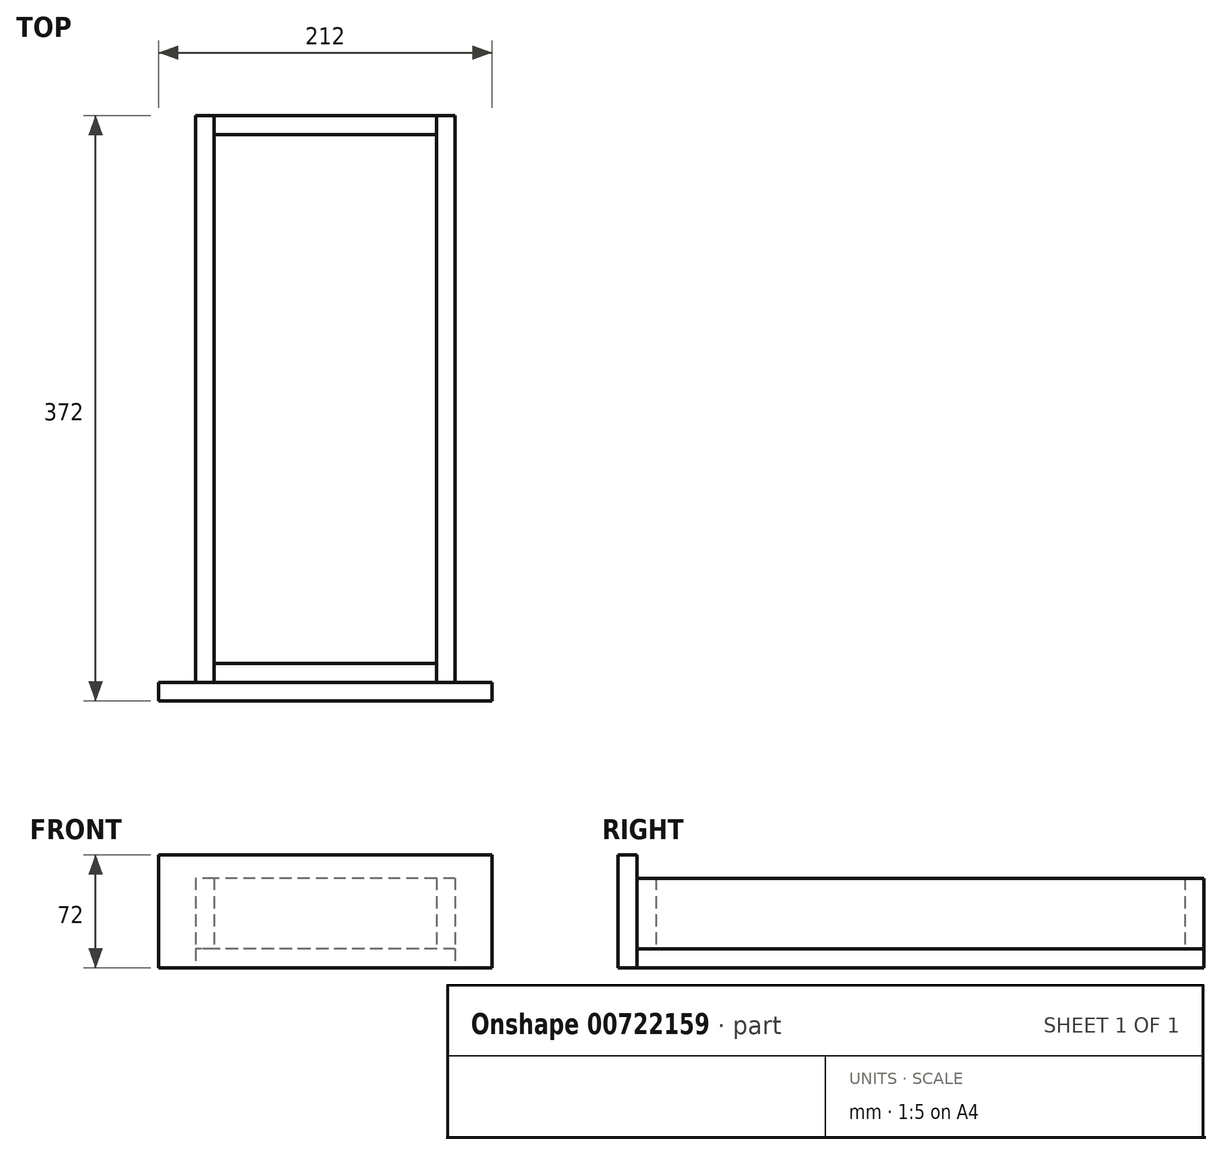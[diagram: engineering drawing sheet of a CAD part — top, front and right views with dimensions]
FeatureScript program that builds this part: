
annotation { "Feature Type Name" : "Feature", "Feature Type Description" : "" }
export const myFeature = defineFeature(function(context is Context, id is Id, definition is map)
    precondition{}
    {
        {
            var Q0;
            Q0=qCreatedBy(makeId("Top.planeOp"),FACE);
            var sketch = newSketch(context, id + "F0", { "sketchPlane" : qUnion([Q0])});
            skLineSegment(sketch, "E0.bottom", {"start": v(82.5, -180) * mm, "end": v(-82.5, -180) * mm});
            skLineSegment(sketch, "E0.top", {"start": v(82.5, 180) * mm, "end": v(-82.5, 180) * mm});
            skLineSegment(sketch, "E0.left", {"start": v(82.5, -180) * mm, "end": v(82.5, 180) * mm});
            skLineSegment(sketch, "E0.right", {"start": v(-82.5, -180) * mm, "end": v(-82.5, 180) * mm});
            skPoint(sketch, "E0.middle", {"position": v(0, 0) * mm});
            skSolve(sketch);
        }
        {
            var Q0;
            Q0 = qSketchRegion(id + "F0", true);
            extrude(context, id + "F1", {"entities" : qUnion([Q0]), "depth" : 12 * mm, "offsetDistance" : 25 * mm});
        }
        {
            var Q0;
            Q0=makeQuery(id+"F1.opExtrude","CAP_FACE",FACE,{"disambiguationData":[OSD([sQuery(id+"F0.wireOp",EDGE,"E0.bottom"),sQuery(id+"F0.wireOp",EDGE,"E0.top"),sQuery(id+"F0.wireOp",EDGE,"E0.left"),sQuery(id+"F0.wireOp",EDGE,"E0.right")])],"isStart":false});
            var sketch = newSketch(context, id + "F2", { "sketchPlane" : qUnion([Q0])});
            skLineSegment(sketch, "E1.0", {"start": v(-82.5, -180) * mm, "end": v(-82.5, 180) * mm});
            skLineSegment(sketch, "E2.0", {"start": v(82.5, 180) * mm, "end": v(-82.5, 180) * mm});
            skLineSegment(sketch, "E3.0", {"start": v(82.5, -180) * mm, "end": v(82.5, 180) * mm});
            skLineSegment(sketch, "E4.0", {"start": v(82.5, -180) * mm, "end": v(-82.5, -180) * mm});
            skLineSegment(sketch, "E5", {"start": v(-70.5, 180) * mm, "end": v(-70.5, -180) * mm});
            skLineSegment(sketch, "E6", {"start": v(70.5, 180) * mm, "end": v(70.5, -180) * mm});
            skLineSegment(sketch, "E7", {"start": v(-70.5, -168) * mm, "end": v(70.5, -168) * mm});
            skLineSegment(sketch, "E8", {"start": v(-70.5, 168) * mm, "end": v(70.5, 168) * mm});
            skSolve(sketch);
        }
        {
            var Q0;
            {var subQ5=sQuery(id+"F2.wireOp",EDGE,"E8");Q0=makeQuery(id+"F2.imprint","IMPRINT",FACE,{"disambiguationData":[TD([[makeQuery(id+"F2.imprint","IMPRINT",EDGE,{"derivedFrom":subQ5}),1.0]])]});}
            var Q1;
            {var subQ5=sQuery(id+"F2.wireOp",EDGE,"E7");Q1=makeQuery(id+"F2.imprint","IMPRINT",FACE,{"disambiguationData":[TD([[makeQuery(id+"F2.imprint","IMPRINT",EDGE,{"derivedFrom":subQ5}),-1.0]])]});}
            extrude(context, id + "F3", {"entities" : qUnion([Q0, Q1]), "depth" : 45 * mm, "offsetDistance" : 25 * mm});
        }
        {
            var Q0;
            {var subQ1=sQuery(id+"F2.wireOp",EDGE,"E1.0");Q0=makeQuery(id+"F2.imprint","IMPRINT",FACE,{"disambiguationData":[TD([[makeQuery(id+"F2.imprint","IMPRINT",EDGE,{"derivedFrom":subQ1}),-1.0]])]});}
            var Q1;
            {var subQ1=sQuery(id+"F2.wireOp",EDGE,"E3.0");Q1=makeQuery(id+"F2.imprint","IMPRINT",FACE,{"disambiguationData":[TD([[makeQuery(id+"F2.imprint","IMPRINT",EDGE,{"derivedFrom":subQ1}),1.0]])]});}
            extrude(context, id + "F4", {"entities" : qUnion([Q0, Q1]), "depth" : 45 * mm, "offsetDistance" : 25 * mm});
        }
        {
            var Q0;
            Q0=makeQuery(id+"F3.opExtrude","SWEPT_FACE",FACE,{"disambiguationData":[OSD([sQuery(id+"F2.wireOp",EDGE,"E4.0")])]});
            var sketch = newSketch(context, id + "F5", { "sketchPlane" : qUnion([Q0])});
            skLineSegment(sketch, "E9.0", {"start": v(82.5, 0) * mm, "end": v(-82.5, 0) * mm});
            skLineSegment(sketch, "E10", {"start": v(-82.5, 0) * mm, "end": v(-106, 0) * mm});
            skLineSegment(sketch, "E11", {"start": v(-106, 0) * mm, "end": v(-106, 72) * mm});
            skLineSegment(sketch, "E12", {"start": v(-106, 72) * mm, "end": v(106, 72) * mm});
            skLineSegment(sketch, "E13", {"start": v(106, 72) * mm, "end": v(106, 0) * mm});
            skLineSegment(sketch, "E14", {"start": v(106, 0) * mm, "end": v(82.5, 0) * mm});
            skSolve(sketch);
        }
        {
            var Q0;
            Q0=makeQuery(id+"F5.imprint","IMPRINT",FACE,{"disambiguationData":[TD([[makeQuery(id+"F5.imprint","IMPRINT",EDGE,{"derivedFrom":sQuery(id+"F5.wireOp",EDGE,"E9.0")}),-1.0]])]});
            var Q1;
            {var subQ0=sQuery(id+"F2.wireOp",EDGE,"E4.0");Q1=makeQuery(id+"F5.imprint","IMPRINT",FACE,{"disambiguationData":[TD([[makeQuery(id+"F5.imprint","IMPRINT",EDGE,{"derivedFrom":makeQuery(id+"F3.opExtrude","CAP_EDGE",EDGE,{"disambiguationData":[OSD([subQ0])],"isStart":true})}),-1.0]])]});}
            extrude(context, id + "F6", {"entities" : qUnion([Q0, Q1]), "depth" : 12 * mm, "offsetDistance" : 25 * mm});
        }
    });
